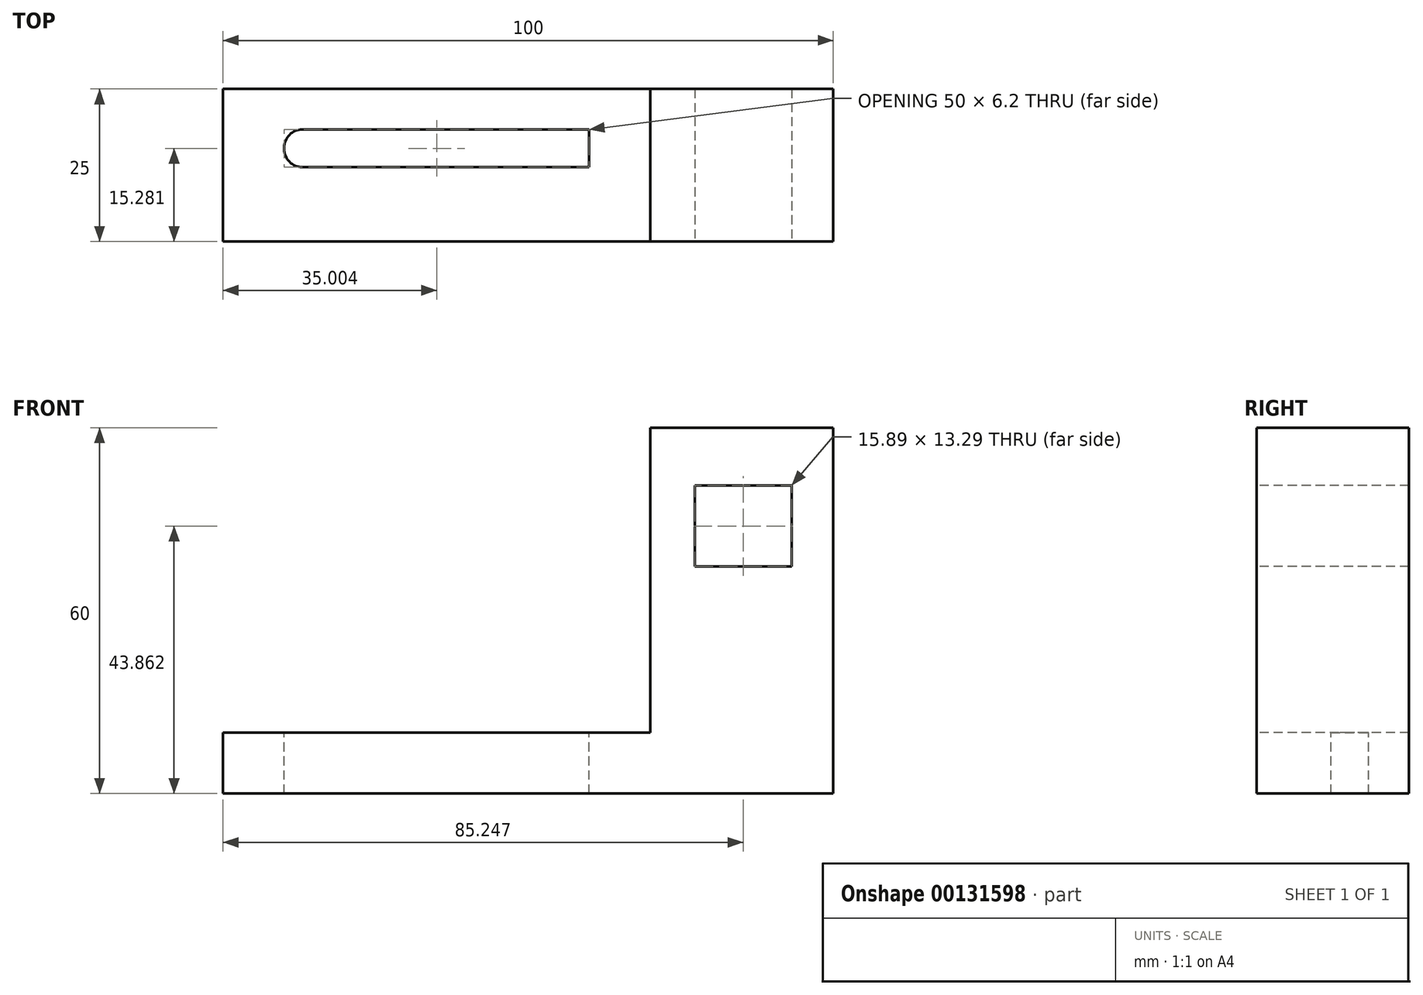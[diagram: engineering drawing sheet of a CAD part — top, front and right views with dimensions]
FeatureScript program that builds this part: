
annotation { "Feature Type Name" : "Feature", "Feature Type Description" : "" }
export const myFeature = defineFeature(function(context is Context, id is Id, definition is map)
    precondition{}
    {
        {
            var Q0;
            Q0=qCreatedBy(makeId("Top.planeOp"),FACE);
            var sketch = newSketch(context, id + "F0", { "sketchPlane" : qUnion([Q0])});
            skLineSegment(sketch, "E0.bottom", {"start": v(-35.9, 28.87) * mm, "end": v(64.1, 28.87) * mm});
            skLineSegment(sketch, "E0.top", {"start": v(-35.9, 53.87) * mm, "end": v(64.1, 53.87) * mm});
            skLineSegment(sketch, "E0.left", {"start": v(-35.9, 28.87) * mm, "end": v(-35.9, 53.87) * mm});
            skLineSegment(sketch, "E0.right", {"start": v(64.1, 28.87) * mm, "end": v(64.1, 53.87) * mm});
            skSolve(sketch);
        }
        {
            var Q0;
            Q0 = qSketchRegion(id + "F0", true);
            extrude(context, id + "F1", {"entities" : qUnion([Q0]), "depth" : 10 * mm});
        }
        {
            var Q0;
            Q0=makeQuery(id+"F1.opExtrude","CAP_FACE",FACE,{"disambiguationData":[OSD([sQuery(id+"F0.wireOp",EDGE,"E0.bottom"),sQuery(id+"F0.wireOp",EDGE,"E0.top"),sQuery(id+"F0.wireOp",EDGE,"E0.left"),sQuery(id+"F0.wireOp",EDGE,"E0.right")])],"isStart":false});
            var sketch = newSketch(context, id + "F2", { "sketchPlane" : qUnion([Q0])});
            skLineSegment(sketch, "E1.bottom", {"start": v(34.1, 53.87) * mm, "end": v(64.1, 53.87) * mm});
            skLineSegment(sketch, "E1.top", {"start": v(34.1, 28.87) * mm, "end": v(64.1, 28.87) * mm});
            skLineSegment(sketch, "E1.left", {"start": v(34.1, 53.87) * mm, "end": v(34.1, 28.87) * mm});
            skLineSegment(sketch, "E1.right", {"start": v(64.1, 53.87) * mm, "end": v(64.1, 28.87) * mm});
            skSolve(sketch);
        }
        {
            var Q0;
            Q0 = qSketchRegion(id + "F2", true);
            extrude(context, id + "F3", {"entities" : qUnion([Q0]), "operationType" : NewBodyOperationType.ADD, "depth" : 50 * mm});
        }
        {
            var Q0;
            Q0=makeQuery(id+"F3.boolean.opBoolean","MERGE",FACE,{"derivedFrom":[makeQuery(id+"F1.opExtrude","SWEPT_FACE",FACE,{"disambiguationData":[OSD([sQuery(id+"F0.wireOp",EDGE,"E0.bottom")])]}),makeQuery(id+"F3.opExtrude","SWEPT_FACE",FACE,{"disambiguationData":[OSD([sQuery(id+"F2.wireOp",EDGE,"E1.top")])]})]});
            var sketch = newSketch(context, id + "F4", { "sketchPlane" : qUnion([Q0])});
            skLineSegment(sketch, "E2.bottom", {"start": v(41.4, 50.5) * mm, "end": v(57.3, 50.5) * mm});
            skLineSegment(sketch, "E2.top", {"start": v(41.4, 37.22) * mm, "end": v(57.3, 37.22) * mm});
            skLineSegment(sketch, "E2.left", {"start": v(41.4, 50.5) * mm, "end": v(41.4, 37.22) * mm});
            skLineSegment(sketch, "E2.right", {"start": v(57.3, 50.5) * mm, "end": v(57.3, 37.22) * mm});
            skSolve(sketch);
        }
        {
            var Q0;
            Q0 = qSketchRegion(id + "F4", true);
            extrude(context, id + "F5", {"entities" : qUnion([Q0]), "operationType" : NewBodyOperationType.REMOVE, "endBound" : BoundingType.THROUGH_ALL, "oppositeDirection" : true, "depth" : 25 * mm});
        }
        {
            var Q0;
            Q0=makeQuery(id+"F1.opExtrude","CAP_FACE",FACE,{"disambiguationData":[OSD([sQuery(id+"F0.wireOp",EDGE,"E0.bottom"),sQuery(id+"F0.wireOp",EDGE,"E0.top"),sQuery(id+"F0.wireOp",EDGE,"E0.left"),sQuery(id+"F0.wireOp",EDGE,"E0.right")])],"isStart":false});
            var sketch = newSketch(context, id + "F6", { "sketchPlane" : qUnion([Q0])});
            skLineSegment(sketch, "E3.bottom", {"start": v(24.1, 41.05) * mm, "end": v(-22.9, 41.05) * mm});
            skLineSegment(sketch, "E3.top", {"start": v(24.1, 47.25) * mm, "end": v(-22.9, 47.25) * mm});
            skLineSegment(sketch, "E3.left", {"start": v(24.1, 41.05) * mm, "end": v(24.1, 47.25) * mm});
            skLineSegment(sketch, "E3.right", {"start": v(-25.9, 44.05) * mm, "end": v(-25.9, 44.25) * mm});
            skPoint(sketch, "E4.visualSharp", {"position": v(-25.9, 41.05) * mm});
            skArc(sketch, "E4.filletArc", {"start": v(-25.9, 44.05) * mm, "mid": v(-25.02, 41.93) * mm, "end": v(-22.9, 41.05) * mm});
            skPoint(sketch, "E5.visualSharp", {"position": v(-25.9, 47.25) * mm});
            skArc(sketch, "E5.filletArc", {"start": v(-22.9, 47.25) * mm, "mid": v(-25.02, 46.37) * mm, "end": v(-25.9, 44.25) * mm});
            skSolve(sketch);
        }
        {
            var Q0;
            Q0 = qSketchRegion(id + "F6", true);
            extrude(context, id + "F7", {"entities" : qUnion([Q0]), "operationType" : NewBodyOperationType.REMOVE, "oppositeDirection" : true, "depth" : 25 * mm});
        }
    });
